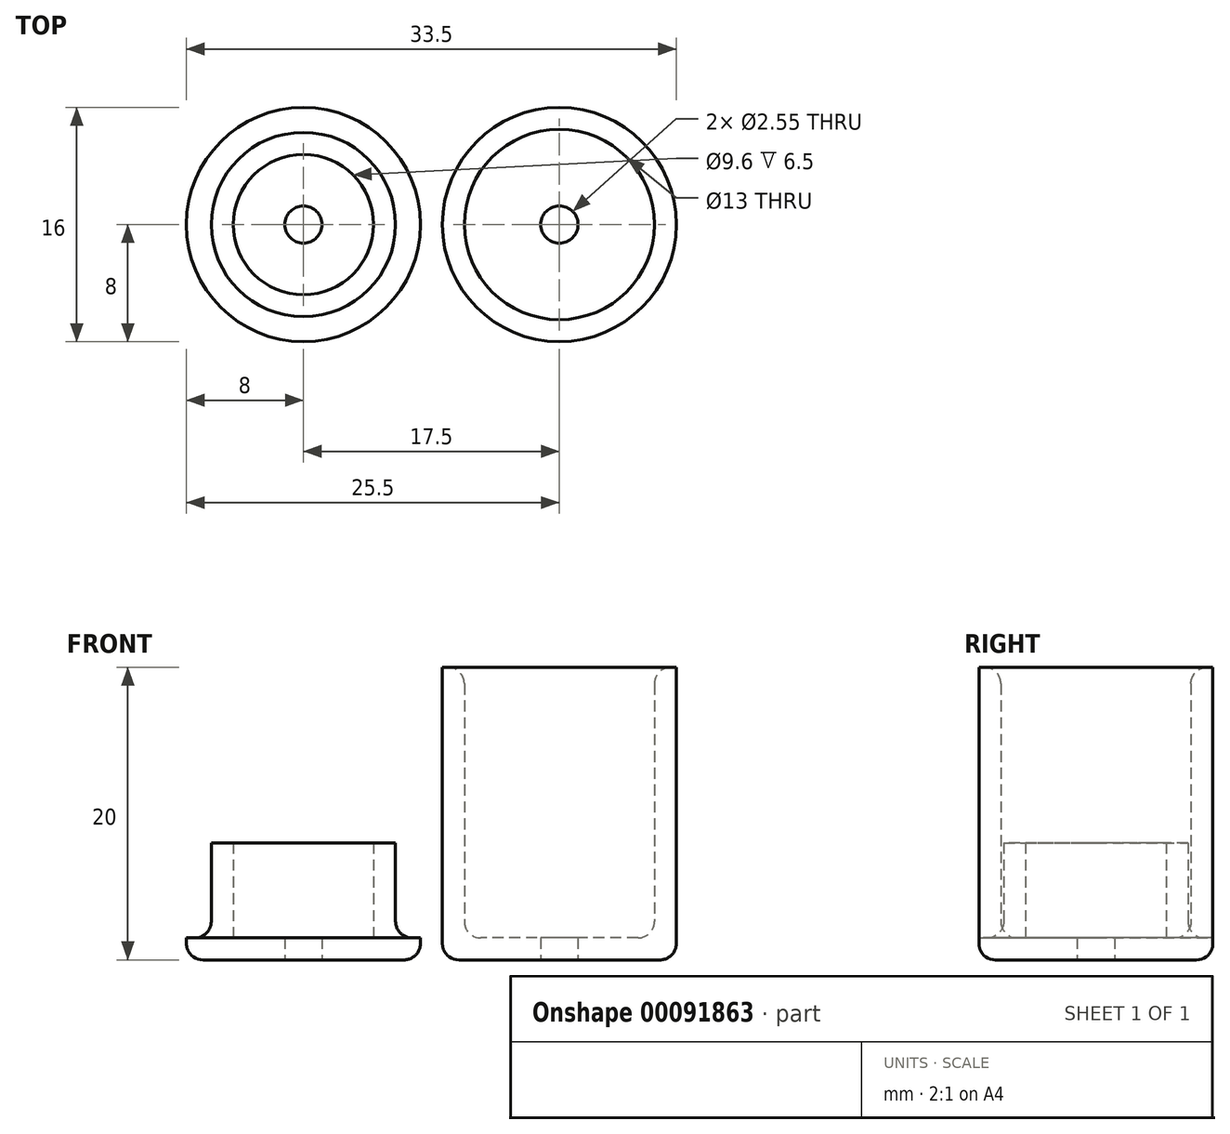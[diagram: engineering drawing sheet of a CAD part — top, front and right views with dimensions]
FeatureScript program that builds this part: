
annotation { "Feature Type Name" : "Feature", "Feature Type Description" : "" }
export const myFeature = defineFeature(function(context is Context, id is Id, definition is map)
    precondition{}
    {
        {
            assignVariable(context, id + "F0", {"name" : "BottomHeight", "anyValue" : 20});
        }
        {
            assignVariable(context, id + "F1", {"name" : "CapHeight", "anyValue" : getVariable(context, 'BottomHeight') * 2 / 5});
        }
        {
            assignVariable(context, id + "F2", {"name" : "Diameter", "anyValue" : 16});
        }
        {
            assignVariable(context, id + "F3", {"name" : "WallThickness", "anyValue" : 1.5});
        }
        {
            var Q0;
            Q0=qCreatedBy(makeId("Top.planeOp"),FACE);
            var sketch = newSketch(context, id + "F4", { "sketchPlane" : qUnion([Q0])});
            skCircle(sketch, "E0", {"center": v(0, 0) * mm, "radius": 1.27 * mm});
            skCircle(sketch, "E1", {"center": v(0, 0) * mm, "radius": 8 * mm});
            skCircle(sketch, "E2.0", {"center": v(0, 0) * mm, "radius": 6.5 * mm});
            skCircle(sketch, "E3.0", {"center": v(0, 0) * mm, "radius": 6.3 * mm});
            skCircle(sketch, "E4.0", {"center": v(0, 0) * mm, "radius": 4.8 * mm});
            skSolve(sketch);
        }
        {
            var Q0;
            Q0=makeQuery(id+"F4.imprint","IMPRINT",FACE,{"disambiguationData":[TD([[makeQuery(id+"F4.imprint","IMPRINT",EDGE,{"derivedFrom":sQuery(id+"F4.wireOp",EDGE,"E1")}),1.0]])]});
            var Q1;
            Q1=makeQuery(id+"F4.imprint","IMPRINT",FACE,{"disambiguationData":[TD([[makeQuery(id+"F4.imprint","IMPRINT",EDGE,{"derivedFrom":sQuery(id+"F4.wireOp",EDGE,"E2.0")}),1.0]])]});
            var Q2;
            Q2=makeQuery(id+"F4.imprint","IMPRINT",FACE,{"disambiguationData":[TD([[makeQuery(id+"F4.imprint","IMPRINT",EDGE,{"derivedFrom":sQuery(id+"F4.wireOp",EDGE,"E0")}),-1.0]])]});
            var Q3;
            Q3=makeQuery(id+"F4.imprint","IMPRINT",FACE,{"disambiguationData":[TD([[makeQuery(id+"F4.imprint","IMPRINT",EDGE,{"derivedFrom":sQuery(id+"F4.wireOp",EDGE,"E3.0")}),1.0]])]});
            extrude(context, id + "F5", {"entities" : qUnion([Q0, Q1, Q2, Q3]), "depth" : (getVariable(context, 'WallThickness')) * mm});
        }
        {
            var Q0;
            Q0=makeQuery(id+"F4.imprint","IMPRINT",FACE,{"disambiguationData":[TD([[makeQuery(id+"F4.imprint","IMPRINT",EDGE,{"derivedFrom":sQuery(id+"F4.wireOp",EDGE,"E1")}),1.0]])]});
            extrude(context, id + "F6", {"entities" : qUnion([Q0]), "operationType" : NewBodyOperationType.ADD, "depth" : (getVariable(context, 'BottomHeight')) * mm});
        }
        {
            var Q0;
            Q0=makeQuery(id+"F5.opExtrude","SWEPT_BODY",BODY,{"disambiguationData":[OSD([sQuery(id+"F4.wireOp",EDGE,"E0"),sQuery(id+"F4.wireOp",EDGE,"E1")])]});
            transform(context, id + "F7", {"entities" : qUnion([Q0]), "transformType" : TransformType.TRANSLATION_3D, "dx" : (getVariable(context, 'Diameter') + getVariable(context, 'WallThickness')) * mm, "dy" : 0 * mm, "dz" : 0 * mm, "makeCopy" : false});
        }
        {
            var Q0;
            Q0=makeQuery(id+"F4.imprint","IMPRINT",FACE,{"disambiguationData":[TD([[makeQuery(id+"F4.imprint","IMPRINT",EDGE,{"derivedFrom":sQuery(id+"F4.wireOp",EDGE,"E2.0")}),1.0]])]});
            var Q1;
            Q1=makeQuery(id+"F4.imprint","IMPRINT",FACE,{"disambiguationData":[TD([[makeQuery(id+"F4.imprint","IMPRINT",EDGE,{"derivedFrom":sQuery(id+"F4.wireOp",EDGE,"E0")}),-1.0]])]});
            var Q2;
            Q2=makeQuery(id+"F4.imprint","IMPRINT",FACE,{"disambiguationData":[TD([[makeQuery(id+"F4.imprint","IMPRINT",EDGE,{"derivedFrom":sQuery(id+"F4.wireOp",EDGE,"E1")}),1.0]])]});
            var Q3;
            Q3=makeQuery(id+"F4.imprint","IMPRINT",FACE,{"disambiguationData":[TD([[makeQuery(id+"F4.imprint","IMPRINT",EDGE,{"derivedFrom":sQuery(id+"F4.wireOp",EDGE,"E3.0")}),1.0]])]});
            extrude(context, id + "F8", {"entities" : qUnion([Q0, Q1, Q2, Q3]), "depth" : (getVariable(context, 'WallThickness')) * mm});
        }
        {
            var Q0;
            Q0=makeQuery(id+"F4.imprint","IMPRINT",FACE,{"disambiguationData":[TD([[makeQuery(id+"F4.imprint","IMPRINT",EDGE,{"derivedFrom":sQuery(id+"F4.wireOp",EDGE,"E3.0")}),1.0]])]});
            extrude(context, id + "F9", {"entities" : qUnion([Q0]), "operationType" : NewBodyOperationType.ADD, "depth" : (getVariable(context, 'CapHeight')) * mm});
        }
        {
            var Q0;
            Q0=makeQuery(id+"F8.opExtrude","CAP_EDGE",EDGE,{"disambiguationData":[OSD([sQuery(id+"F4.wireOp",EDGE,"E1")])],"isStart":true});
            var Q1;
            Q1=makeQuery(id+"F5.opExtrude","CAP_EDGE",EDGE,{"disambiguationData":[OSD([sQuery(id+"F4.wireOp",EDGE,"E1")])],"isStart":true});
            var Q2;
            Q2=makeQuery(id+"F9.opExtrude","CAP_EDGE",EDGE,{"disambiguationData":[OSD([sQuery(id+"F4.wireOp",EDGE,"E2.0")])],"isStart":false});
            var Q3;
            Q3=makeQuery(id+"F6.opExtrude","CAP_EDGE",EDGE,{"disambiguationData":[OSD([sQuery(id+"F4.wireOp",EDGE,"E2.0")])],"isStart":false});
            var Q4;
            Q4=makeQuery(id+"F6.boolean.opBoolean","INTERSECT",EDGE,{"derivedFrom":[makeQuery(id+"F5.opExtrude","CAP_FACE",FACE,{"disambiguationData":[OSD([sQuery(id+"F4.wireOp",EDGE,"E0"),sQuery(id+"F4.wireOp",EDGE,"E1")])],"isStart":false}),makeQuery(id+"F6.opExtrude","SWEPT_FACE",FACE,{"disambiguationData":[OSD([sQuery(id+"F4.wireOp",EDGE,"E2.0")])]})]});
            var Q5;
            Q5=makeQuery(id+"F9.boolean.opBoolean","INTERSECT",EDGE,{"derivedFrom":[makeQuery(id+"F8.opExtrude","CAP_FACE",FACE,{"disambiguationData":[OSD([sQuery(id+"F4.wireOp",EDGE,"E0"),sQuery(id+"F4.wireOp",EDGE,"E1")])],"isStart":false}),makeQuery(id+"F9.opExtrude","SWEPT_FACE",FACE,{"disambiguationData":[OSD([sQuery(id+"F4.wireOp",EDGE,"E3.0")])]})]});
            fillet(context, id + "F10", {"entities" : qUnion([Q0, Q1, Q2, Q3, Q4, Q5]), "radius" : (getVariable(context, 'WallThickness') * 3 / 4) * mm, "tangentPropagation" : true, "allowEdgeOverflow" : false});
        }
    });
